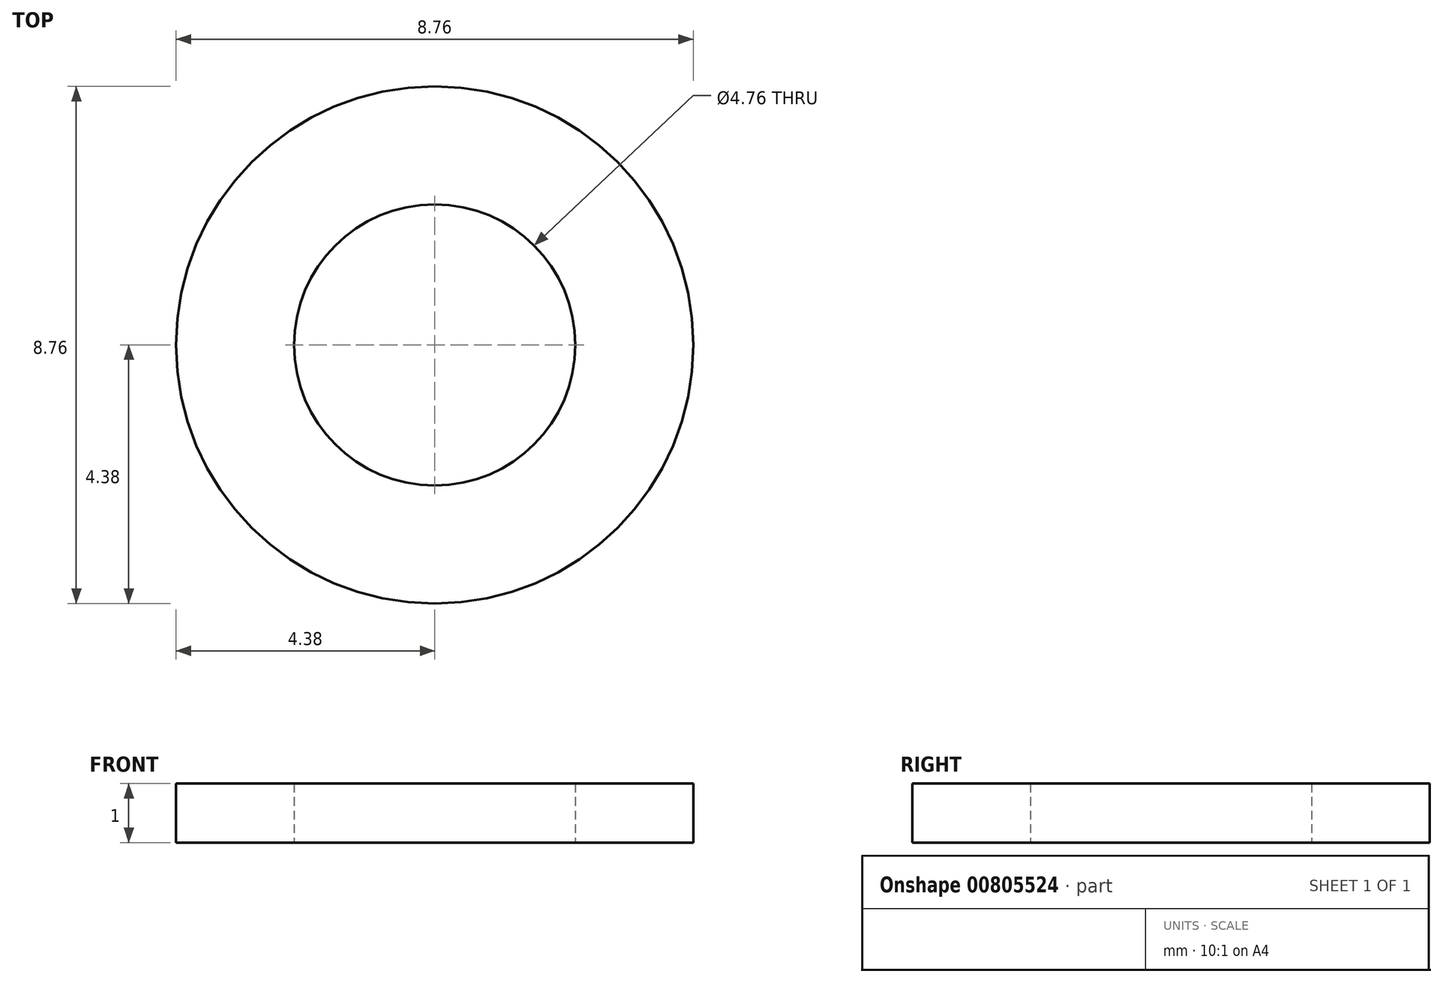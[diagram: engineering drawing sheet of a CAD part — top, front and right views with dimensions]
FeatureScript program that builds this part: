
annotation { "Feature Type Name" : "Feature", "Feature Type Description" : "" }
export const myFeature = defineFeature(function(context is Context, id is Id, definition is map)
    precondition{}
    {
        {
            var Q0;
            Q0=qCreatedBy(makeId("Top.planeOp"),FACE);
            var sketch = newSketch(context, id + "F0", { "sketchPlane" : qUnion([Q0])});
            skCircle(sketch, "E0", {"center": v(0, 0) * mm, "radius": 2.38 * mm});
            skCircle(sketch, "E1", {"center": v(0, 0) * mm, "radius": 4.38 * mm});
            skSolve(sketch);
        }
        {
            var Q0;
            Q0=makeQuery(id+"F0.imprint","IMPRINT",FACE,{"disambiguationData":[TD([[makeQuery(id+"F0.imprint","IMPRINT",EDGE,{"derivedFrom":sQuery(id+"F0.wireOp",EDGE,"E0")}),-1.0]])]});
            extrude(context, id + "F1", {"entities" : qUnion([Q0]), "depth" : 1 * mm, "offsetDistance" : 25 * mm});
        }
    });
